# Revit family: Hager-VEGAD-Flush_mounted-IP40-With_Cover-With_DIN-Hosted-BE-en
name_source: partatom
category: Electrical Equipment
units: mm (PartAtom-declared; Revit-internal decimal feet)

## family parameters
Cut with Voids When Loaded = No
Host = Face
Maintain Annotation Orientation = Yes
Panel Configuration = Two Columns, Circuits Across
Part Type = Panelboard
Room Calculation Point = No
Round Connector Dimension = Use Diameter
Shared = No

## types (12) — shared parameters
BC_MODEL_ID = 1546992
BC_OBJECT_ID = 513429
BC_OBJECT_VERSION = #5
Code hager = ADD-EC000214_EU
EF000003 - Mounting method = Flush-mounted
EF000008 - Width = 600 mm
EF000024 - UV resistant = No
EF000049 - Depth = 150 mm  [stored 0.492126 ft]
EF000116 - RAL-number = 9010
EF000118 - With mounting plate = No
EF000218 - Built-in depth = 150 mm  [stored 0.492126 ft]
EF000846 - Built-in width = 550 mm
EF001062 - EMC-version = No
EF001134 - DIN-rail = Yes
EF002950 - Width in number of modular spacings = 24
EF005474 - Degree of protection (IP) = IP40
EF006306 - With lock = No
EF015777 - Neutral terminal block = No
EF015941 - Signal passing door = No
ETIM class code = EC000214
ETIM class name = Small distribution board
HG000001-Number of columns = 1
HG000002-With door or cover = Yes
HG000003-Range = VEGAD
HG000005-Thickness = 2 mm  [stored 0.00656168 ft]
HG000006-Flush mounted = Yes
HG000009-Double swing door = No
HG000010-Asymmetric doors = No
HG000011-Empty rows from bottom = No
HG000012-Door swing angle = 90.00°
HG000013-Door on the left = No
HG000014-Door on the right = Yes
HG000015-Clearance visibility = Yes
HG000016-Door 3D visibility = Yes
HG000017-Distance between poles = 18 mm  [stored 0.0590551 ft]
HG000060-RAL-number = 9010
HG000099-Onfly Template ID = 507532
HGEF002950-Width in number of modular spacings = 24
Manufacturer = Hager
Name = VEGAD-Flush_mounted-IP40-With_Cover-With_DIN-BE
Name BIM&CO = Electricity
Name hager = ADD_Enclosures_EC000214
Uniformat = Low Tension Service & Dist.
Uniformat code = D501001
zero-valued in all types: Default Elevation, EF001131 - Inner depth, HG000007-Number of empty columns, HG000008-Number of empty rows

## per-type parameters (varying)
| type | BC_VARIANT_ID | EF000007 - Colour | EF000040 - Height | EF000266 - Number of rows | EF000332 - Built-in height | EF001088 - Extension possible | EF004462 - Type of closure | EF006244 - Transparent cover/door | EF009212 - Cover model | EF015776 - Earthing terminal block | HG000004-Manufacturer reference | HGEF000266-Number of rows |
| VEGAD-Flush_mounted_W600_H537_D150_24_Modular_Spacing-FU22BN | 1173848 | White | 537 mm  [stored 1.76181 ft] | 2 | 537 mm  [stored 1.76181 ft] | Yes | Other | No | Closed | No | FU22BN | 2 |
| VEGAD-Flush_mounted_W600_H537_D150_24_Modular_Spacing-FU22CN | 1173849 | White | 537 mm  [stored 1.76181 ft] | 2 | 537 mm  [stored 1.76181 ft] | Yes | Other | Yes | With notch | No | FU22CN | 2 |
| VEGAD-Flush_mounted_W600_H687_D150_24_Modular_Spacing-FU32BN | 1173850 | White | 687 mm  [stored 2.25394 ft] | 3 | 687 mm  [stored 2.25394 ft] | Yes | Other | No | Closed | No | FU32BN | 3 |
| VEGAD-Flush_mounted_W600_H687_D150_24_Modular_Spacing-FU32CN | 1173851 | White | 687 mm  [stored 2.25394 ft] | 3 | 687 mm  [stored 2.25394 ft] | Yes | Other | Yes | With notch | No | FU32CN | 3 |
| VEGAD-Flush_mounted_W600_H837_D150_24_Modular_Spacing-FU42BN | 1173852 | White | 837 mm  [stored 2.74606 ft] | 4 | 837 mm  [stored 2.74606 ft] | Yes | Other | No | Closed | No | FU42BN | 4 |
| VEGAD-Flush_mounted_W600_H837_D150_24_Modular_Spacing-FU42CN | 1173853 | White | 837 mm  [stored 2.74606 ft] | 4 | 837 mm  [stored 2.74606 ft] | Yes | Other | Yes | With notch | No | FU42CN | 4 |
| VEGAD-Flush_mounted_W600_H987_D150_24_Modular_Spacing-FU52BN | 1173854 | White | 987 mm  [stored 3.23819 ft] | 5 | 987 mm  [stored 3.23819 ft] | Yes | Other | No | Closed | No | FU52BN | 5 |
| VEGAD-Flush_mounted_W600_H987_D150_24_Modular_Spacing-FU52CN | 1173855 |  | 987 mm  [stored 3.23819 ft] | 5 | 987 mm  [stored 3.23819 ft] | No |  | Yes | With notch | Yes | FU52CN | 5 |
| VEGAD-Flush_mounted_W600_H1137_D150_24_Modular_Spacing-FU62BN | 1173856 |  | 1137 mm  [stored 3.73031 ft] | 6 | 1137 mm  [stored 3.73031 ft] | No |  | No | With notch | Yes | FU62BN | 6 |
| VEGAD-Flush_mounted_W600_H1137_D150_24_Modular_Spacing-FU62CN | 1173857 |  | 1137 mm  [stored 3.73031 ft] | 6 | 1137 mm  [stored 3.73031 ft] | No |  | Yes | With notch | Yes | FU62CN | 6 |
| VEGAD-Flush_mounted_W600_H1287_D150_24_Modular_Spacing-FU72BN | 1173858 |  | 1287 mm  [stored 4.22244 ft] | 7 | 1287 mm  [stored 4.22244 ft] | No |  | No | With notch | Yes | FU72BN | 7 |
| VEGAD-Flush_mounted_W600_H1287_D150_24_Modular_Spacing-FU72CN | 1173859 |  | 1287 mm  [stored 4.22244 ft] | 7 | 1287 mm  [stored 4.22244 ft] | No |  | Yes | With notch | Yes | FU72CN | 7 |

note: column(s) folded — value = type name in every type: Reference

note: [stored X ft] marks values corroborated as IEEE doubles in the binary element streams (Revit-internal decimal feet)

## geometry (parser evidence)
native form markers: Sweep x16
no freeform markers — native parametric forms only
